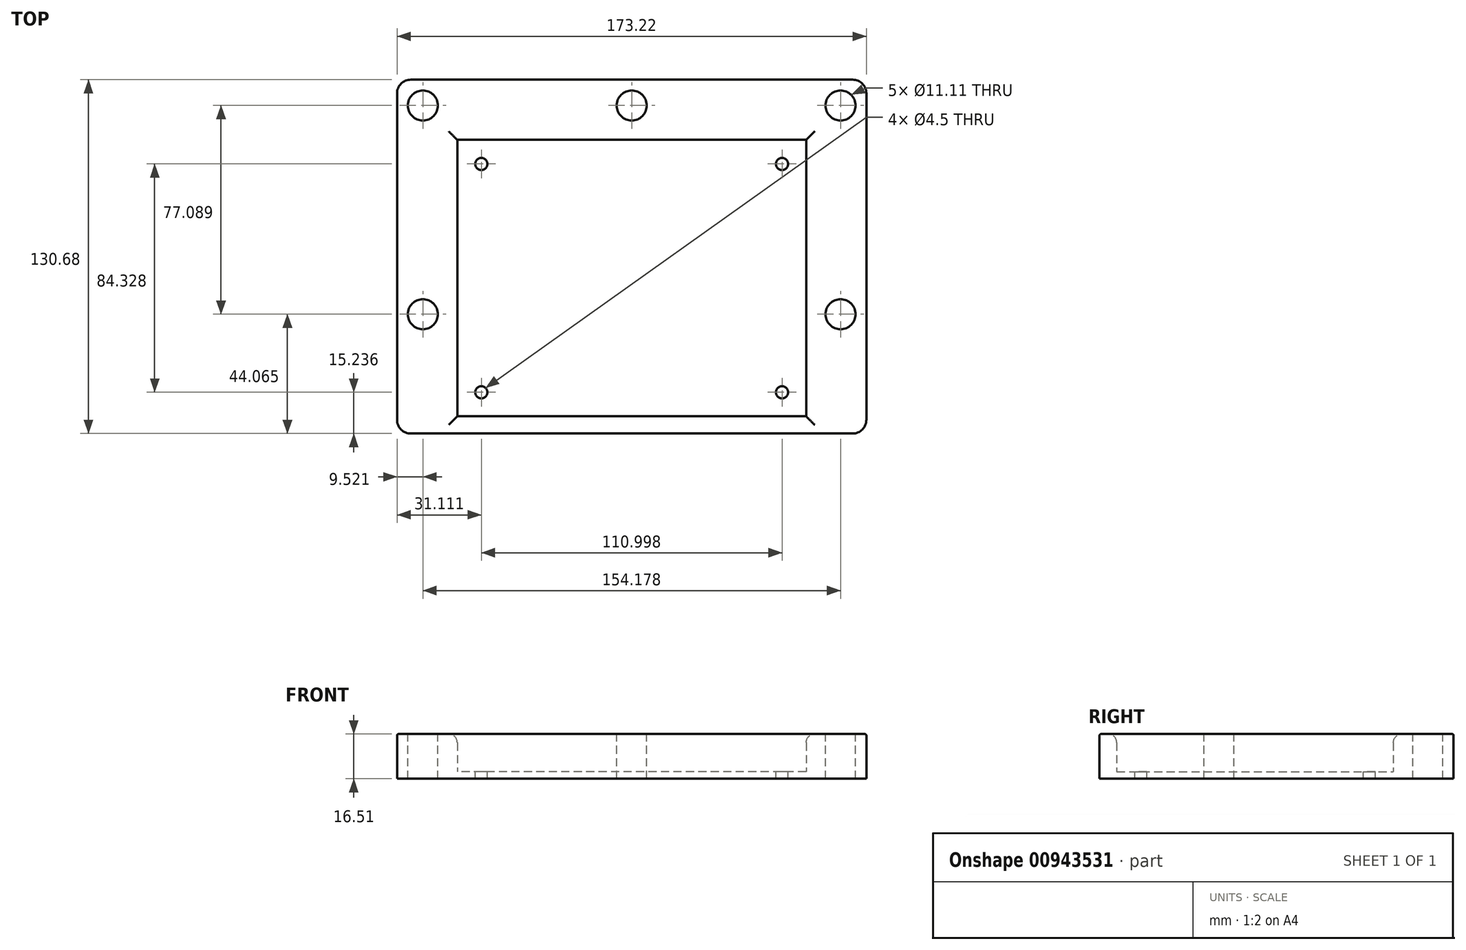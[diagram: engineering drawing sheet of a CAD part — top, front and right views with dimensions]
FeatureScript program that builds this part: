
annotation { "Feature Type Name" : "Feature", "Feature Type Description" : "" }
export const myFeature = defineFeature(function(context is Context, id is Id, definition is map)
    precondition{}
    {
        {
            var Q0;
            Q0=qCreatedBy(makeId("Top.planeOp"),FACE);
            var sketch = newSketch(context, id + "F0", { "sketchPlane" : qUnion([Q0])});
            skLineSegment(sketch, "E0.bottom", {"start": v(64.39, -51.05) * mm, "end": v(-64.39, -51.05) * mm});
            skLineSegment(sketch, "E0.top", {"start": v(64.39, 51.05) * mm, "end": v(-64.39, 51.05) * mm});
            skLineSegment(sketch, "E0.left", {"start": v(64.39, -51.05) * mm, "end": v(64.39, 51.05) * mm});
            skLineSegment(sketch, "E0.right", {"start": v(-64.39, -51.05) * mm, "end": v(-64.39, 51.05) * mm});
            skPoint(sketch, "E0.middle", {"position": v(0, 0) * mm});
            skSolve(sketch);
        }
        {
            var Q0;
            Q0=makeQuery(id+"F0.imprint","IMPRINT",FACE,{"disambiguationData":[TD([[makeQuery(id+"F0.imprint","IMPRINT",EDGE,{"derivedFrom":sQuery(id+"F0.wireOp",EDGE,"E0.bottom")}),-1.0]])]});
            extrude(context, id + "F1", {"entities" : qUnion([Q0]), "depth" : 2.54 * mm, "offsetDistance" : 25.4 * mm});
        }
        {
            var Q0;
            Q0=qCreatedBy(makeId("Top.planeOp"),FACE);
            var sketch = newSketch(context, id + "F2", { "sketchPlane" : qUnion([Q0])});
            skLineSegment(sketch, "E1.bottom", {"start": v(86.61, -57.4) * mm, "end": v(-86.61, -57.4) * mm});
            skLineSegment(sketch, "E1.top", {"start": v(86.61, 73.28) * mm, "end": v(-86.61, 73.28) * mm});
            skLineSegment(sketch, "E1.left", {"start": v(86.61, -57.4) * mm, "end": v(86.61, 73.28) * mm});
            skLineSegment(sketch, "E1.right", {"start": v(-86.61, -57.4) * mm, "end": v(-86.61, 73.28) * mm});
            skPoint(sketch, "E1.middle", {"position": v(0, 24.78) * mm});
            skLineSegment(sketch, "E2.bottom", {"start": v(64.39, -51.05) * mm, "end": v(-64.39, -51.05) * mm});
            skLineSegment(sketch, "E2.top", {"start": v(64.39, 51.05) * mm, "end": v(-64.39, 51.05) * mm});
            skLineSegment(sketch, "E2.left", {"start": v(64.39, -51.05) * mm, "end": v(64.39, 51.05) * mm});
            skLineSegment(sketch, "E2.right", {"start": v(-64.39, -51.05) * mm, "end": v(-64.39, 51.05) * mm});
            skPoint(sketch, "E2.middle", {"position": v(0, 0) * mm});
            skSolve(sketch);
        }
        {
            var Q0;
            Q0=makeQuery(id+"F2.imprint","IMPRINT",FACE,{"disambiguationData":[TD([[makeQuery(id+"F2.imprint","IMPRINT",EDGE,{"derivedFrom":sQuery(id+"F2.wireOp",EDGE,"E1.bottom")}),-1.0]])]});
            extrude(context, id + "F3", {"entities" : qUnion([Q0]), "operationType" : NewBodyOperationType.ADD, "depth" : 16.5 * mm, "offsetDistance" : 25.4 * mm});
        }
        {
            var Q0;
            Q0=makeQuery(id+"F3.opExtrude","CAP_EDGE",EDGE,{"disambiguationData":[OSD([sQuery(id+"F2.wireOp",EDGE,"E2.right")])],"isStart":false});
            var Q1;
            Q1=makeQuery(id+"F3.opExtrude","CAP_EDGE",EDGE,{"disambiguationData":[OSD([sQuery(id+"F2.wireOp",EDGE,"E2.top")])],"isStart":false});
            var Q2;
            Q2=makeQuery(id+"F3.opExtrude","CAP_EDGE",EDGE,{"disambiguationData":[OSD([sQuery(id+"F2.wireOp",EDGE,"E2.left")])],"isStart":false});
            var Q3;
            Q3=makeQuery(id+"F3.opExtrude","CAP_EDGE",EDGE,{"disambiguationData":[OSD([sQuery(id+"F2.wireOp",EDGE,"E2.bottom")])],"isStart":false});
            fillet(context, id + "F4", {"entities" : qUnion([Q0, Q1, Q2, Q3]), "radius" : 3.17 * mm, "tangentPropagation" : true, "allowEdgeOverflow" : false});
        }
        {
            var Q0;
            Q0=makeQuery(id+"F3.opExtrude","CAP_FACE",FACE,{"disambiguationData":[OSD([sQuery(id+"F2.wireOp",EDGE,"E1.bottom"),sQuery(id+"F2.wireOp",EDGE,"E1.top"),sQuery(id+"F2.wireOp",EDGE,"E1.left"),sQuery(id+"F2.wireOp",EDGE,"E1.right"),sQuery(id+"F2.wireOp",EDGE,"E2.bottom"),sQuery(id+"F2.wireOp",EDGE,"E2.top"),sQuery(id+"F2.wireOp",EDGE,"E2.left"),sQuery(id+"F2.wireOp",EDGE,"E2.right")])],"isStart":false});
            var sketch = newSketch(context, id + "F5", { "sketchPlane" : qUnion([Q0])});
            skCircle(sketch, "E3", {"center": v(0, 63.75) * mm, "radius": 5.56 * mm});
            skCircle(sketch, "E4", {"center": v(77.09, 63.75) * mm, "radius": 5.56 * mm});
            skCircle(sketch, "E5", {"center": v(-77.09, 63.75) * mm, "radius": 5.56 * mm});
            skCircle(sketch, "E6", {"center": v(-77.09, -13.34) * mm, "radius": 5.56 * mm});
            skCircle(sketch, "E7", {"center": v(77.09, -13.33) * mm, "radius": 5.56 * mm});
            skLineSegment(sketch, "E8", {"start": v(-67.56, 7.94) * mm, "end": v(-86.61, 7.94) * mm, "construction": true});
            skLineSegment(sketch, "E9", {"start": v(67.56, 7.94) * mm, "end": v(86.61, 7.94) * mm, "construction": true});
            skPoint(sketch, "E10", {"position": v(-77.09, 7.94) * mm});
            skPoint(sketch, "E11", {"position": v(77.09, 7.94) * mm});
            skLineSegment(sketch, "E12", {"start": v(-77.09, 63.75) * mm, "end": v(0, 63.75) * mm, "construction": true});
            skLineSegment(sketch, "E13", {"start": v(-77.09, 63.75) * mm, "end": v(-77.09, -13.34) * mm, "construction": true});
            skLineSegment(sketch, "E14", {"start": v(0, 73.28) * mm, "end": v(0, 54.23) * mm, "construction": true});
            skSolve(sketch);
        }
        {
            var Q0;
            Q0 = qSketchRegion(id + "F5", true);
            extrude(context, id + "F6", {"entities" : qUnion([Q0]), "operationType" : NewBodyOperationType.REMOVE, "endBound" : BoundingType.THROUGH_ALL, "oppositeDirection" : true, "depth" : 11.43 * mm, "offsetDistance" : 25.4 * mm});
        }
        {
            var Q0;
            Q0=makeQuery(id+"F1.opExtrude","CAP_FACE",FACE,{"disambiguationData":[OSD([sQuery(id+"F0.wireOp",EDGE,"E0.bottom"),sQuery(id+"F0.wireOp",EDGE,"E0.top"),sQuery(id+"F0.wireOp",EDGE,"E0.left"),sQuery(id+"F0.wireOp",EDGE,"E0.right")])],"isStart":false});
            var sketch = newSketch(context, id + "F7", { "sketchPlane" : qUnion([Q0])});
            skCircle(sketch, "E15", {"center": v(-55.5, 42.16) * mm, "radius": 2.25 * mm});
            skCircle(sketch, "E16", {"center": v(55.5, 42.16) * mm, "radius": 2.25 * mm});
            skCircle(sketch, "E17", {"center": v(55.5, -42.16) * mm, "radius": 2.25 * mm});
            skCircle(sketch, "E18", {"center": v(-55.5, -42.16) * mm, "radius": 2.25 * mm});
            skLineSegment(sketch, "E19", {"start": v(-55.5, 42.16) * mm, "end": v(55.5, -42.16) * mm, "construction": true});
            skLineSegment(sketch, "E20", {"start": v(55.5, 42.16) * mm, "end": v(-55.5, -42.16) * mm, "construction": true});
            skLineSegment(sketch, "E21", {"start": v(-55.5, 42.16) * mm, "end": v(-55.5, 51.05) * mm, "construction": true});
            skLineSegment(sketch, "E22", {"start": v(-55.5, 51.05) * mm, "end": v(-55.5, 42.16) * mm, "construction": true});
            skLineSegment(sketch, "E23", {"start": v(-55.5, 42.16) * mm, "end": v(-64.39, 42.16) * mm, "construction": true});
            skSolve(sketch);
        }
        {
            var Q0;
            Q0 = qSketchRegion(id + "F7", true);
            extrude(context, id + "F8", {"entities" : qUnion([Q0]), "operationType" : NewBodyOperationType.REMOVE, "endBound" : BoundingType.THROUGH_ALL, "oppositeDirection" : true, "depth" : 25.4 * mm, "offsetDistance" : 25.4 * mm});
        }
        {
            var Q0;
            Q0=makeQuery(id+"F3.opExtrude","CAP_EDGE",EDGE,{"disambiguationData":[OSD([sQuery(id+"F2.wireOp",EDGE,"E1.top")])],"isStart":false});
            var Q1;
            Q1=makeQuery(id+"F3.opExtrude","CAP_EDGE",EDGE,{"disambiguationData":[OSD([sQuery(id+"F2.wireOp",EDGE,"E1.right")])],"isStart":false});
            var Q2;
            Q2=makeQuery(id+"F3.opExtrude","CAP_EDGE",EDGE,{"disambiguationData":[OSD([sQuery(id+"F2.wireOp",EDGE,"E1.bottom")])],"isStart":false});
            var Q3;
            Q3=makeQuery(id+"F3.opExtrude","CAP_EDGE",EDGE,{"disambiguationData":[OSD([sQuery(id+"F2.wireOp",EDGE,"E1.left")])],"isStart":false});
            fillet(context, id + "F9", {"entities" : qUnion([Q0, Q1, Q2, Q3]), "radius" : 0.5 * mm, "tangentPropagation" : true, "allowEdgeOverflow" : false});
        }
        {
            var Q0;
            Q0=makeQuery(id+"F3.opExtrude","SWEPT_EDGE",EDGE,{"disambiguationData":[OSD([sQuery(id+"F2.wireOp",EDGE,"E1.top"),sQuery(id+"F2.wireOp",EDGE,"E1.right")])]});
            var Q1;
            Q1=makeQuery(id+"F3.opExtrude","SWEPT_EDGE",EDGE,{"disambiguationData":[OSD([sQuery(id+"F2.wireOp",EDGE,"E1.bottom"),sQuery(id+"F2.wireOp",EDGE,"E1.right")])]});
            var Q2;
            Q2=makeQuery(id+"F3.opExtrude","SWEPT_EDGE",EDGE,{"disambiguationData":[OSD([sQuery(id+"F2.wireOp",EDGE,"E1.bottom"),sQuery(id+"F2.wireOp",EDGE,"E1.left")])]});
            var Q3;
            Q3=makeQuery(id+"F3.opExtrude","SWEPT_EDGE",EDGE,{"disambiguationData":[OSD([sQuery(id+"F2.wireOp",EDGE,"E1.top"),sQuery(id+"F2.wireOp",EDGE,"E1.left")])]});
            fillet(context, id + "F10", {"entities" : qUnion([Q0, Q1, Q2, Q3]), "radius" : 5.08 * mm, "tangentPropagation" : true, "allowEdgeOverflow" : false});
        }
    });
